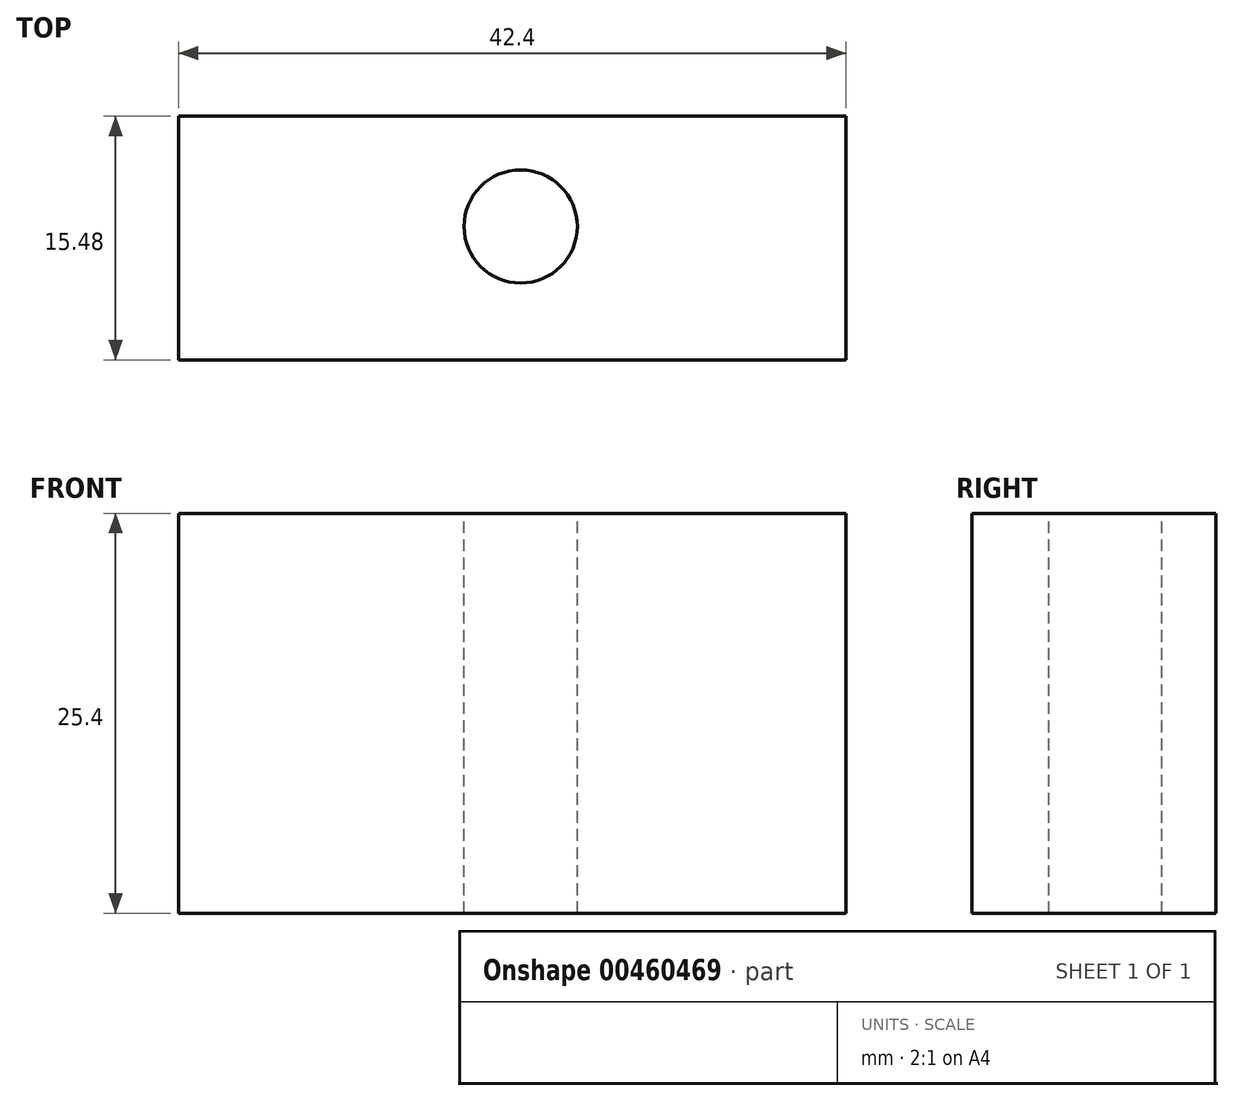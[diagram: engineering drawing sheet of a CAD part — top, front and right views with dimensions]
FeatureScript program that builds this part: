
annotation { "Feature Type Name" : "Feature", "Feature Type Description" : "" }
export const myFeature = defineFeature(function(context is Context, id is Id, definition is map)
    precondition{}
    {
        {
            var Q0;
            Q0=qCreatedBy(makeId("Top.planeOp"),FACE);
            var sketch = newSketch(context, id + "F0", { "sketchPlane" : qUnion([Q0])});
            skLineSegment(sketch, "E0.bottom", {"start": v(0, 0) * mm, "end": v(68.37, 0) * mm});
            skLineSegment(sketch, "E0.top", {"start": v(0, -34) * mm, "end": v(68.37, -34) * mm});
            skLineSegment(sketch, "E0.left", {"start": v(0, 0) * mm, "end": v(0, -34) * mm});
            skLineSegment(sketch, "E0.right", {"start": v(68.37, 0) * mm, "end": v(68.37, -34) * mm});
            skSolve(sketch);
        }
        {
            var Q0;
            Q0=makeQuery(id+"F0.imprint","IMPRINT",FACE,{"disambiguationData":[TD([[makeQuery(id+"F0.imprint","IMPRINT",EDGE,{"derivedFrom":sQuery(id+"F0.wireOp",EDGE,"E0.bottom")}),-1.0]])]});
            var sketch = newSketch(context, id + "F1", { "sketchPlane" : qUnion([Q0])});
            skCircle(sketch, "E1", {"center": v(33.02, -14.5) * mm, "radius": 6.12 * mm});
            skCircle(sketch, "E2", {"center": v(33.02, -14.5) * mm, "radius": 3.97 * mm});
            skSolve(sketch);
        }
        {
            var Q0;
            Q0=makeQuery(id+"F0.imprint","IMPRINT",FACE,{"disambiguationData":[TD([[makeQuery(id+"F0.imprint","IMPRINT",EDGE,{"derivedFrom":sQuery(id+"F0.wireOp",EDGE,"E0.bottom")}),-1.0]])]});
            extrude(context, id + "F2", {"entities" : qUnion([Q0]), "oppositeDirection" : true, "depth" : 25.4 * mm});
        }
        {
            var Q0;
            Q0=sQuery(id+"F1.wireOp",VERTEX,"E2.center");
            var Q1;
            Q1=makeQuery(id+"F2.opExtrude","SWEPT_BODY",BODY,{"disambiguationData":[OSD([sQuery(id+"F0.wireOp",EDGE,"E0.bottom"),sQuery(id+"F0.wireOp",EDGE,"E0.top"),sQuery(id+"F0.wireOp",EDGE,"E0.left"),sQuery(id+"F0.wireOp",EDGE,"E0.right")])]});
            hole(context, id + "F3", {"style" : HoleStyle.C_BORE, "endStyle" : HoleEndStyle.THROUGH, "holeDiameter" : 6.35 * mm, "cBoreDiameter" : 7.62 * mm, "cBoreDepth" : 9.52 * mm, "isTappedThrough" : true, "tappedDepth" : 12.7 * mm, "tapClearance" : 3, "locations" : qUnion([Q0]), "scope" : qUnion([Q1])});
        }
        {
            var Q0;
            Q0=makeQuery(id+"F2.opExtrude","CAP_FACE",FACE,{"disambiguationData":[OSD([sQuery(id+"F0.wireOp",EDGE,"E0.bottom"),sQuery(id+"F0.wireOp",EDGE,"E0.top"),sQuery(id+"F0.wireOp",EDGE,"E0.left"),sQuery(id+"F0.wireOp",EDGE,"E0.right")])],"isStart":true});
            var sketch = newSketch(context, id + "F4", { "sketchPlane" : qUnion([Q0])});
            skCircle(sketch, "E3", {"center": v(33.02, -14.5) * mm, "radius": 9.73 * mm});
            skSolve(sketch);
        }
        {
            var Q0;
            Q0=sQuery(id+"F4.wireOp",VERTEX,"E3.center");
            var Q1;
            Q1=makeQuery(id+"F2.opExtrude","SWEPT_BODY",BODY,{"disambiguationData":[OSD([sQuery(id+"F0.wireOp",EDGE,"E0.bottom"),sQuery(id+"F0.wireOp",EDGE,"E0.top"),sQuery(id+"F0.wireOp",EDGE,"E0.left"),sQuery(id+"F0.wireOp",EDGE,"E0.right")])]});
            hole(context, id + "F5", {"style" : HoleStyle.C_BORE, "endStyle" : HoleEndStyle.THROUGH, "holeDiameter" : 19.05 * mm, "cBoreDiameter" : 25.4 * mm, "cBoreDepth" : 6.35 * mm, "isTappedThrough" : true, "tappedDepth" : 12.7 * mm, "tapClearance" : 3, "locations" : qUnion([Q0]), "scope" : qUnion([Q1])});
        }
        {
            var Q0;
            Q0=makeQuery(id+"F2.opExtrude","SWEPT_BODY",BODY,{"disambiguationData":[OSD([sQuery(id+"F0.wireOp",EDGE,"E0.bottom"),sQuery(id+"F0.wireOp",EDGE,"E0.top"),sQuery(id+"F0.wireOp",EDGE,"E0.left"),sQuery(id+"F0.wireOp",EDGE,"E0.right")])]});
            deleteBodies(context, id + "F6", {"entities" : qUnion([Q0])});
        }
        {
            var Q0;
            Q0=qCreatedBy(makeId("Top.planeOp"),FACE);
            var sketch = newSketch(context, id + "F7", { "sketchPlane" : qUnion([Q0])});
            skLineSegment(sketch, "E4.bottom", {"start": v(0, 0) * mm, "end": v(42.4, 0) * mm});
            skLineSegment(sketch, "E4.top", {"start": v(0, -15.48) * mm, "end": v(42.4, -15.48) * mm});
            skLineSegment(sketch, "E4.left", {"start": v(0, 0) * mm, "end": v(0, -15.48) * mm});
            skLineSegment(sketch, "E4.right", {"start": v(42.4, 0) * mm, "end": v(42.4, -15.48) * mm});
            skSolve(sketch);
        }
        {
            var Q0;
            Q0=makeQuery(id+"F7.imprint","IMPRINT",FACE,{"disambiguationData":[TD([[makeQuery(id+"F7.imprint","IMPRINT",EDGE,{"derivedFrom":sQuery(id+"F7.wireOp",EDGE,"E4.bottom")}),-1.0]])]});
            var sketch = newSketch(context, id + "F8", { "sketchPlane" : qUnion([Q0])});
            skCircle(sketch, "E5", {"center": v(21.73, -7) * mm, "radius": 3.6 * mm});
            skSolve(sketch);
        }
        {
            var Q0;
            Q0 = qSketchRegion(id + "F8", true);
            var Q1;
            Q1=makeQuery(id+"F7.imprint","IMPRINT",FACE,{"disambiguationData":[TD([[makeQuery(id+"F7.imprint","IMPRINT",EDGE,{"derivedFrom":sQuery(id+"F7.wireOp",EDGE,"E4.bottom")}),-1.0]])]});
            extrude(context, id + "F9", {"entities" : qUnion([Q0, Q1]), "oppositeDirection" : true, "depth" : 25.4 * mm});
        }
    });
